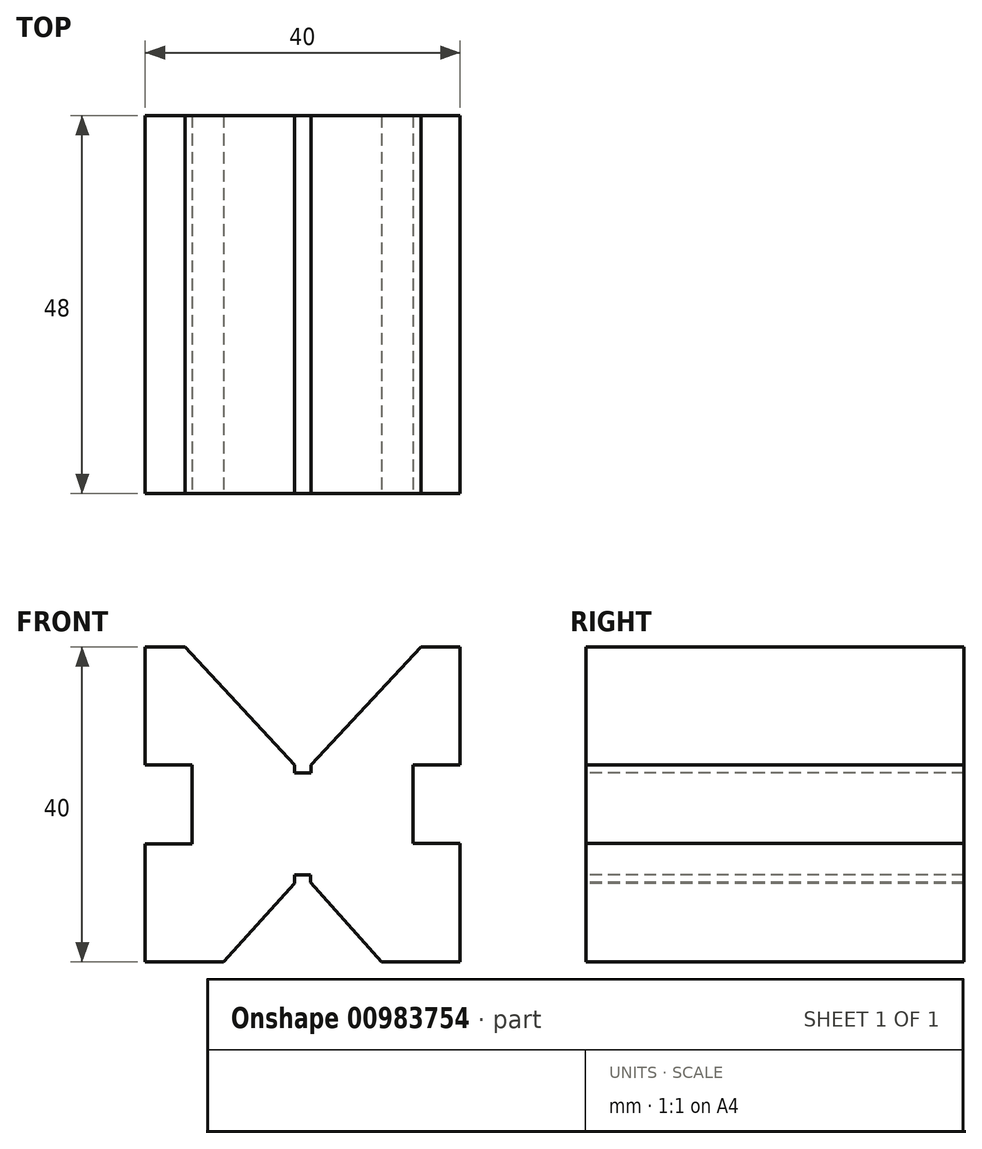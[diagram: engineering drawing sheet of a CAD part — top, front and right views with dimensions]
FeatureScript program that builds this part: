
annotation { "Feature Type Name" : "Feature", "Feature Type Description" : "" }
export const myFeature = defineFeature(function(context is Context, id is Id, definition is map)
    precondition{}
    {
        {
            var Q0;
            Q0=qCreatedBy(makeId("Front.planeOp"),FACE);
            var sketch = newSketch(context, id + "F0", { "sketchPlane" : qUnion([Q0])});
            skLineSegment(sketch, "E0.bottom", {"start": v(0, 0) * mm, "end": v(40, 0) * mm});
            skLineSegment(sketch, "E0.top", {"start": v(0, 40) * mm, "end": v(5.03, 40) * mm});
            skLineSegment(sketch, "E0.left", {"start": v(0, 0) * mm, "end": v(0, 40) * mm});
            skLineSegment(sketch, "E0.right", {"start": v(40, 0) * mm, "end": v(40, 40) * mm});
            skLineSegment(sketch, "E1", {"start": v(0, 40) * mm, "end": v(0, 25) * mm});
            skLineSegment(sketch, "E2", {"start": v(0, 25) * mm, "end": v(5.98, 25) * mm});
            skLineSegment(sketch, "E3", {"start": v(5.98, 25) * mm, "end": v(5.98, 15) * mm});
            skLineSegment(sketch, "E4", {"start": v(0, 15) * mm, "end": v(5.98, 15) * mm});
            skLineSegment(sketch, "E5", {"start": v(5.03, 40) * mm, "end": v(35.05, 40) * mm});
            skLineSegment(sketch, "E6", {"start": v(35.05, 40) * mm, "end": v(40, 40) * mm});
            skLineSegment(sketch, "E7", {"start": v(5.03, 40) * mm, "end": v(20.04, 40) * mm});
            skLineSegment(sketch, "E8", {"start": v(20.04, 40) * mm, "end": v(20.04, 24) * mm});
            skLineSegment(sketch, "E9", {"start": v(20.04, 24) * mm, "end": v(21.04, 24) * mm});
            skLineSegment(sketch, "E10", {"start": v(21.04, 24) * mm, "end": v(20.04, 24) * mm});
            skLineSegment(sketch, "E11", {"start": v(20.04, 24) * mm, "end": v(19, 24) * mm});
            skLineSegment(sketch, "E12", {"start": v(21.04, 24) * mm, "end": v(21.04, 25.03) * mm});
            skLineSegment(sketch, "E13", {"start": v(19, 24) * mm, "end": v(19, 25.03) * mm});
            skLineSegment(sketch, "E14", {"start": v(19, 25.03) * mm, "end": v(5.03, 40) * mm});
            skLineSegment(sketch, "E15", {"start": v(35.05, 40) * mm, "end": v(21.04, 25.03) * mm});
            skLineSegment(sketch, "E16", {"start": v(40, 40) * mm, "end": v(40, 25.03) * mm});
            skLineSegment(sketch, "E17", {"start": v(40, 25.03) * mm, "end": v(34.02, 25.03) * mm});
            skLineSegment(sketch, "E18", {"start": v(34.02, 25.03) * mm, "end": v(34.02, 15.03) * mm});
            skLineSegment(sketch, "E19", {"start": v(34.02, 15.03) * mm, "end": v(40, 15.03) * mm});
            skLineSegment(sketch, "E20", {"start": v(40, 0) * mm, "end": v(30, 0) * mm});
            skLineSegment(sketch, "E21", {"start": v(0, 0) * mm, "end": v(9.98, 0) * mm});
            skLineSegment(sketch, "E22", {"start": v(20, 0) * mm, "end": v(20, 11.03) * mm});
            skLineSegment(sketch, "E23", {"start": v(20, 11.03) * mm, "end": v(19, 11.03) * mm});
            skLineSegment(sketch, "E24", {"start": v(19, 11.03) * mm, "end": v(20, 11.03) * mm});
            skLineSegment(sketch, "E25", {"start": v(20, 11.03) * mm, "end": v(20.99, 11.03) * mm});
            skLineSegment(sketch, "E26", {"start": v(20.99, 11.03) * mm, "end": v(20.99, 10.07) * mm});
            skLineSegment(sketch, "E27", {"start": v(19, 11.03) * mm, "end": v(19, 9.99) * mm});
            skLineSegment(sketch, "E28", {"start": v(19, 9.99) * mm, "end": v(9.98, 0) * mm});
            skLineSegment(sketch, "E29", {"start": v(20.99, 10.07) * mm, "end": v(30, 0) * mm});
            skSolve(sketch);
        }
        {
            var Q0;
            {var subQ3=sQuery(id+"F0.wireOp",EDGE,"E0.top");Q0=makeQuery(id+"F0.imprint","IMPRINT",FACE,{"disambiguationData":[TD([[makeQuery(id+"F0.imprint","IMPRINT",EDGE,{"derivedFrom":subQ3}),-1.0]])]});}
            extrude(context, id + "F1", {"entities" : qUnion([Q0]), "oppositeDirection" : true, "depth" : 48 * mm, "offsetDistance" : 25 * mm});
        }
    });
